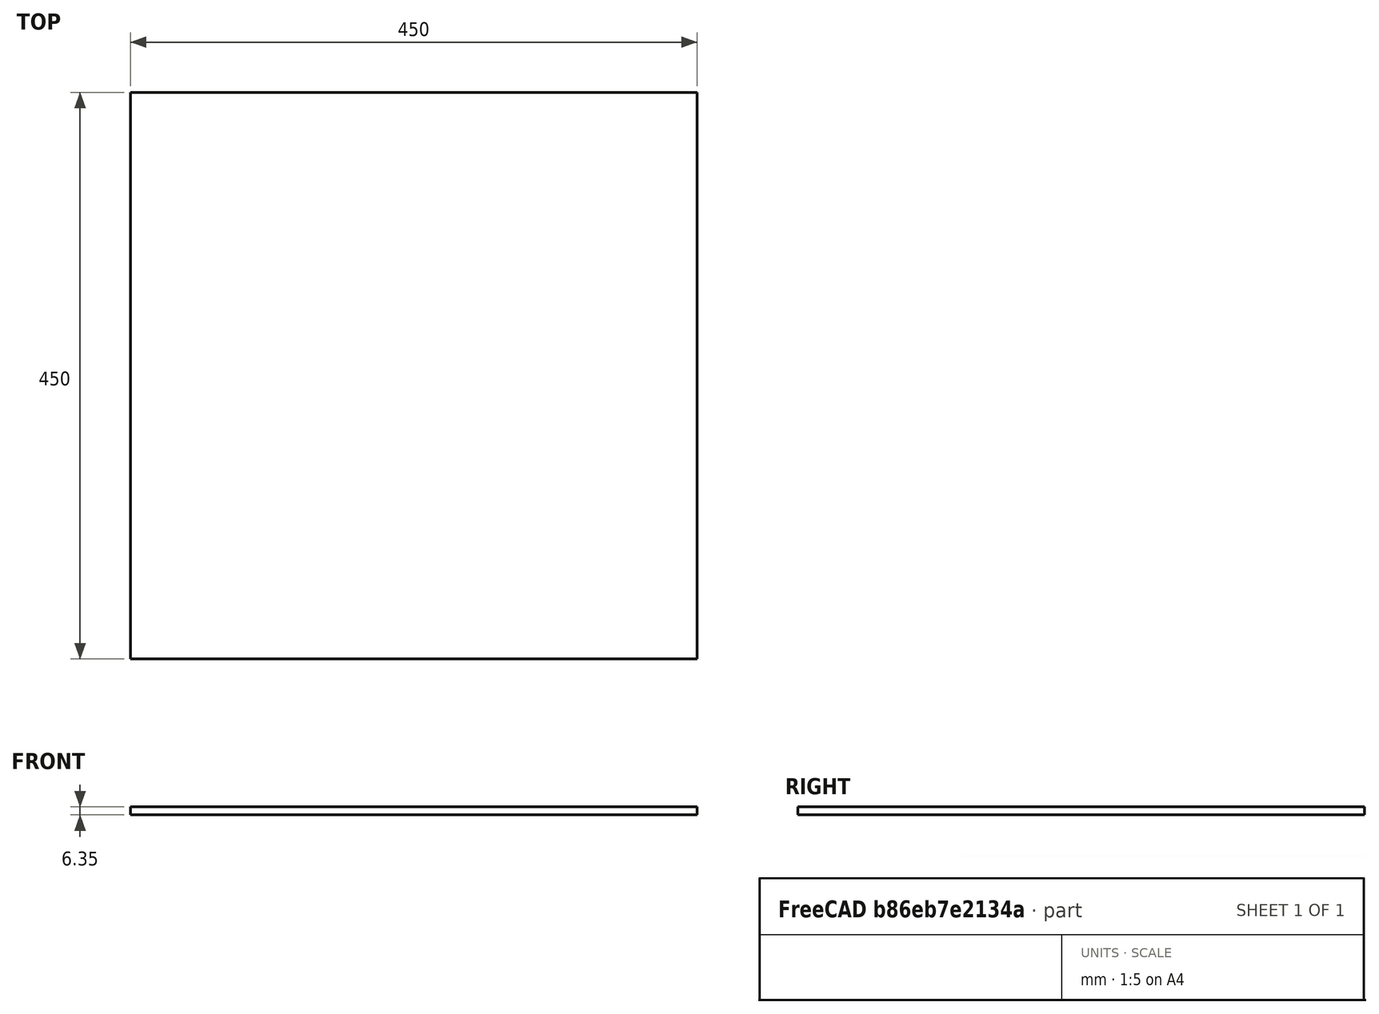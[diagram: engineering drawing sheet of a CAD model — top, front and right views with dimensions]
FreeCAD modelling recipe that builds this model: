
FCSTD DOCUMENT  (FreeCAD 0.16RUnknown)
Label: Base
License: All rights reserved
LicenseURL: http://berserk.design
objects: Sketcher::SketchObject×1, PartDesign::Pad×1
note: 3 computed .brp shape members not serialized (recipe doc carries the construction recipe); baked Part::Feature solids carry a one-line shape summary decoded from their .brp

FEATURE [Sketcher::SketchObject] Sketch
  sketch-geometry (4):
    g0: LineSegment StartX=0 StartY=0 StartZ=0 EndX=450 EndY=0 EndZ=0
    g1: LineSegment StartX=450 StartY=0 StartZ=0 EndX=450 EndY=450 EndZ=0
    g2: LineSegment StartX=450 StartY=450 StartZ=0 EndX=0 EndY=450 EndZ=0
    g3: LineSegment StartX=0 StartY=450 StartZ=0 EndX=0 EndY=0 EndZ=0
  constraints (11):
    c: Coincident(g0,g1)
    c: Coincident(g1,g2)
    c: Coincident(g2,g3)
    c: Coincident(g3,g0)
    c: Horizontal(g0)
    c: Horizontal(g2)
    c: Vertical(g1)
    c: Vertical(g3)
    c: Coincident(g0,g-1)
    c: DistanceX(g2,g2) = 450
    c: DistanceY(g3,g3) = 450
FEATURE [PartDesign::Pad] Pad
  Length = 6.35
  Length2 = 100
  Sketch = -> Sketch
  Type = 0
